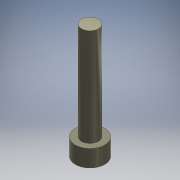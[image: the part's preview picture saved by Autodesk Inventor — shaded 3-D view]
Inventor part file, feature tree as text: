
AUTODESK INVENTOR PART (.ipt)
format: ipt  version: 2016 (Build 200138000, 138)  size: 98,816 bytes
history: native  units: mm
features: extrude x2, sketch x2, other x1
ambient origin geometry x8: Origin, YZ Plane, XZ Plane, XY Plane, X Axis, Y Axis, Z Axis, Center Point
bodies: Body1 (feature_tree)
feature tree (5):
  other  "ソリッド1"
  extrude  "押し出し1"  Depth=4.5mm
  extrude  "押し出し2"  Depth=2.6mm TaperAngle=0.0deg
  sketch  "スケッチ1"
  sketch  "スケッチ2"
